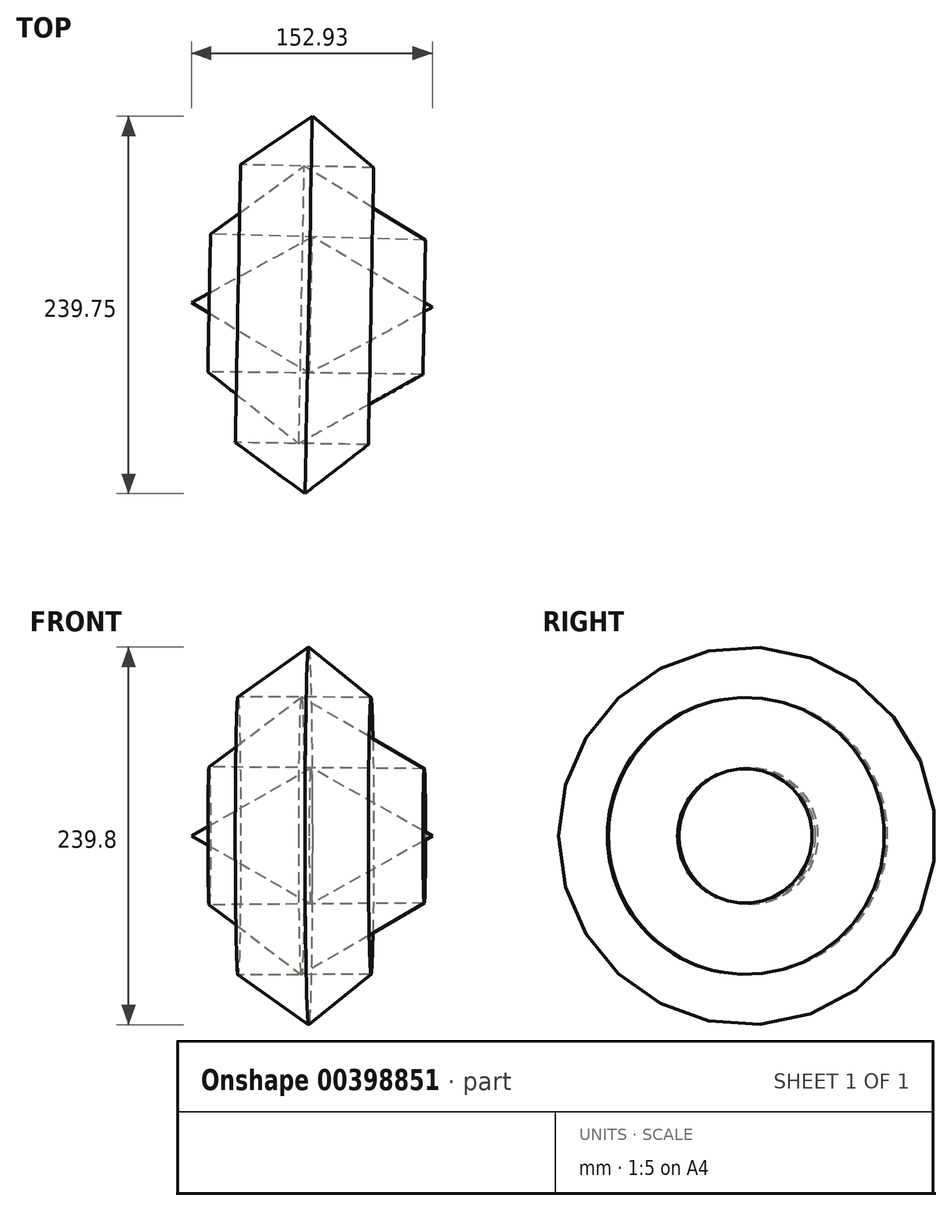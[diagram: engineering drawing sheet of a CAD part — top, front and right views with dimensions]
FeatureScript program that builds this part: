
annotation { "Feature Type Name" : "Feature", "Feature Type Description" : "" }
export const myFeature = defineFeature(function(context is Context, id is Id, definition is map)
    precondition{}
    {
        {
            var Q0;
            Q0=qCreatedBy(makeId("Top.planeOp"),FACE);
            var sketch = newSketch(context, id + "F0", { "sketchPlane" : qUnion([Q0])});
            skLineSegment(sketch, "E0", {"start": v(0, 70.75) * mm, "end": v(-45.52, 40) * mm});
            skLineSegment(sketch, "E1", {"start": v(0, 70.75) * mm, "end": v(39.02, 38.03) * mm});
            skLineSegment(sketch, "E2", {"start": v(-45.52, 40) * mm, "end": v(40.4, 38.03) * mm});
            skLineSegment(sketch, "E3", {"start": v(-5.1, 39.08) * mm, "end": v(-64.64, -4.14) * mm});
            skLineSegment(sketch, "E4", {"start": v(-5.1, 39.08) * mm, "end": v(71.93, -7.88) * mm});
            skLineSegment(sketch, "E5", {"start": v(-64.64, -4.14) * mm, "end": v(71.93, -7.88) * mm});
            skLineSegment(sketch, "E6", {"start": v(0, -5.91) * mm, "end": v(-76.66, -47.7) * mm});
            skLineSegment(sketch, "E7", {"start": v(0, -5.91) * mm, "end": v(76.27, -50.65) * mm});
            skLineSegment(sketch, "E8", {"start": v(-76.66, -47.7) * mm, "end": v(76.27, -50.65) * mm});
            skLineSegment(sketch, "E9", {"start": v(-5.1, 39.08) * mm, "end": v(0, 38.96) * mm});
            skLineSegment(sketch, "E10", {"start": v(0, 70.75) * mm, "end": v(0, -49.17) * mm});
            skSolve(sketch);
        }
        {
            var Q0;
            {var subQ0=sQuery(id+"F0.wireOp",EDGE,"E0");Q0=makeQuery(id+"F0.imprint","IMPRINT",FACE,{"disambiguationData":[TD([[makeQuery(id+"F0.imprint","IMPRINT",EDGE,{"derivedFrom":subQ0}),1.0]])]});}
            var Q1;
            {var subQ1=sQuery(id+"F0.wireOp",EDGE,"E1");var subQ3=sQuery(id+"F0.wireOp",EDGE,"E2");var subQ4=makeQuery(id+"F0.imprint","INTERSECT",VERTEX,{"derivedFrom":[subQ1,subQ3]});Q1=makeQuery(id+"F0.imprint","IMPRINT",FACE,{"disambiguationData":[TD([[makeQuery(id+"F0.imprint","IMPRINT",EDGE,{"disambiguationData":[TD([[subQ4,1.0]])],"derivedFrom":subQ1}),-1.0]])]});}
            var Q2;
            {var subQ0=sQuery(id+"F0.wireOp",EDGE,"E5");var subQ1=sQuery(id+"F0.wireOp",EDGE,"E4");var subQ2=makeQuery(id+"F0.imprint","INTERSECT",VERTEX,{"derivedFrom":[subQ1,subQ0]});Q2=makeQuery(id+"F0.imprint","IMPRINT",FACE,{"disambiguationData":[TD([[makeQuery(id+"F0.imprint","IMPRINT",EDGE,{"disambiguationData":[TD([[subQ2,1.0]])],"derivedFrom":subQ1}),-1.0]])]});}
            var Q3;
            {var subQ0=sQuery(id+"F0.wireOp",EDGE,"E3");Q3=makeQuery(id+"F0.imprint","IMPRINT",FACE,{"disambiguationData":[TD([[makeQuery(id+"F0.imprint","IMPRINT",EDGE,{"derivedFrom":subQ0}),1.0]])]});}
            var Q4;
            {var subQ0=sQuery(id+"F0.wireOp",EDGE,"E7");Q4=makeQuery(id+"F0.imprint","IMPRINT",FACE,{"disambiguationData":[TD([[makeQuery(id+"F0.imprint","IMPRINT",EDGE,{"derivedFrom":subQ0}),-1.0]])]});}
            var Q5;
            {var subQ0=sQuery(id+"F0.wireOp",EDGE,"E6");Q5=makeQuery(id+"F0.imprint","IMPRINT",FACE,{"disambiguationData":[TD([[makeQuery(id+"F0.imprint","IMPRINT",EDGE,{"derivedFrom":subQ0}),1.0]])]});}
            var Q6;
            Q6=sQuery(id+"F0.wireOp",EDGE,"E8");
            revolve(context, id + "F1", {"entities" : qUnion([Q0, Q1, Q2, Q3, Q4, Q5]), "axis" : qUnion([Q6]), "revolveType" : RevolveType.FULL});
        }
    });
